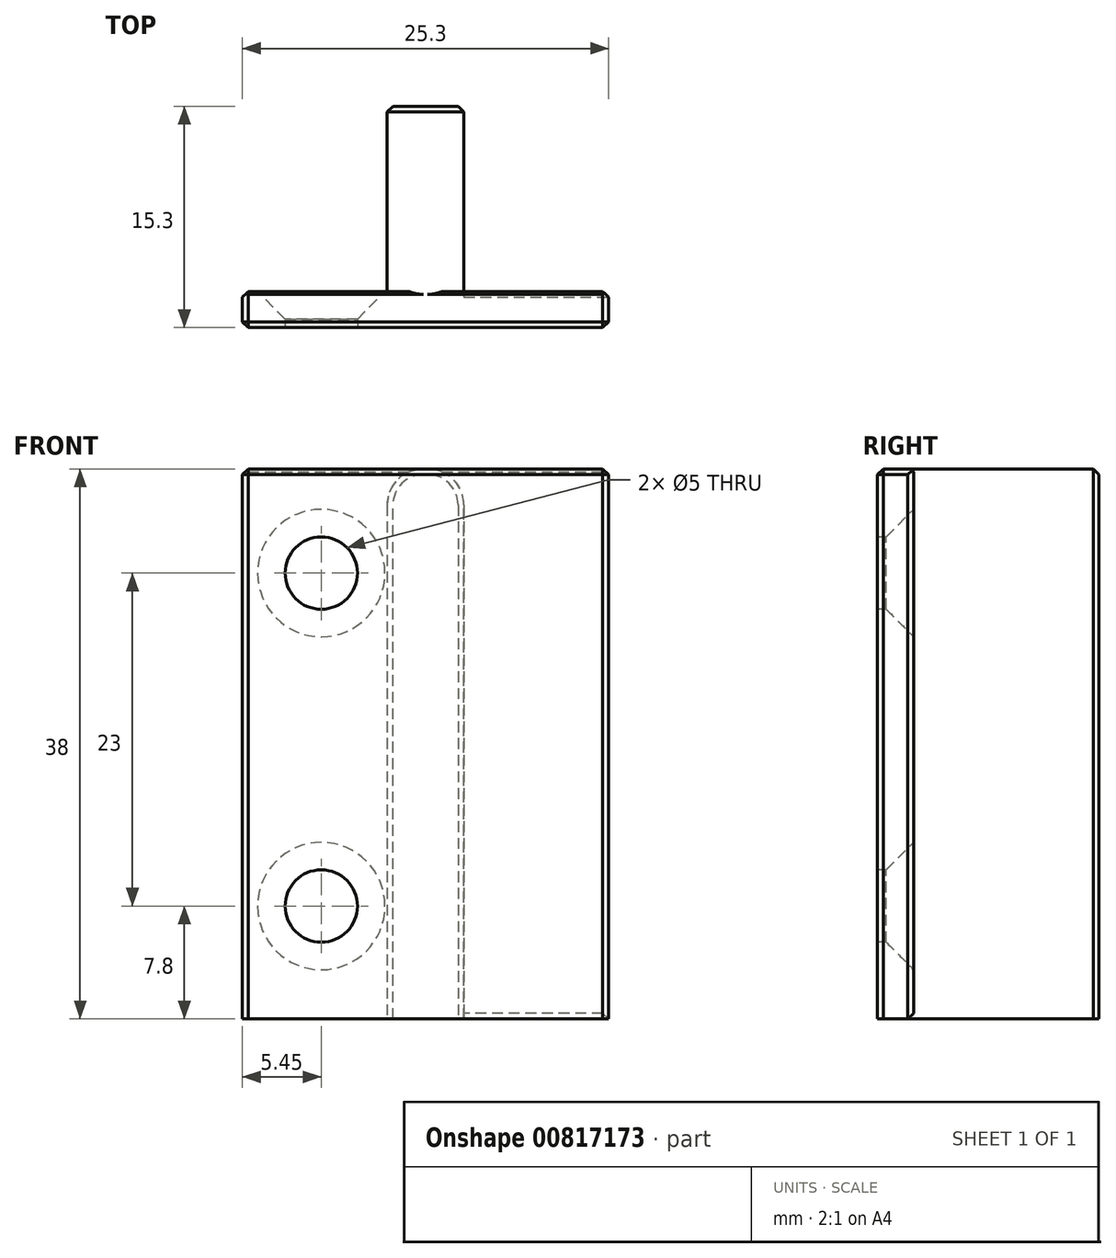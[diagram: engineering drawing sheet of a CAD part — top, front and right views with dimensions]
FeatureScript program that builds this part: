
annotation { "Feature Type Name" : "Feature", "Feature Type Description" : "" }
export const myFeature = defineFeature(function(context is Context, id is Id, definition is map)
    precondition{}
    {
        {
            var Q0;
            Q0=qCreatedBy(makeId("Top.planeOp"),FACE);
            var sketch = newSketch(context, id + "F0", { "sketchPlane" : qUnion([Q0])});
            skLineSegment(sketch, "E0", {"start": v(0, 15.3) * mm, "end": v(-2.65, 15.3) * mm});
            skLineSegment(sketch, "E1", {"start": v(-2.65, 15.3) * mm, "end": v(-2.65, 2.5) * mm});
            skLineSegment(sketch, "E2", {"start": v(-2.65, 2.5) * mm, "end": v(-12.65, 2.5) * mm});
            skLineSegment(sketch, "E3", {"start": v(-12.65, 2.5) * mm, "end": v(-12.65, 0) * mm});
            skLineSegment(sketch, "E4", {"start": v(-12.65, 0) * mm, "end": v(0, 0) * mm});
            skLineSegment(sketch, "E5", {"start": v(0, 26.2) * mm, "end": v(0, -20.62) * mm, "construction": true});
            skLineSegment(sketch, "E6.MirrorCS", {"start": v(0, 15.3) * mm, "end": v(2.65, 15.3) * mm});
            skLineSegment(sketch, "E7.MirrorCS", {"start": v(2.65, 15.3) * mm, "end": v(2.65, 2.5) * mm});
            skLineSegment(sketch, "E8.MirrorCS", {"start": v(2.65, 2.5) * mm, "end": v(12.65, 2.5) * mm});
            skLineSegment(sketch, "E9.MirrorCS", {"start": v(12.65, 0) * mm, "end": v(0, 0) * mm});
            skLineSegment(sketch, "E10.MirrorCS", {"start": v(12.65, 2.5) * mm, "end": v(12.65, 0) * mm});
            skLineSegment(sketch, "E11", {"start": v(-7.2, 6.99) * mm, "end": v(-7.2, -6.23) * mm, "construction": true});
            skSolve(sketch);
        }
        {
            var Q0;
            Q0=makeQuery(id+"F0.imprint","IMPRINT",FACE,{"disambiguationData":[TD([[makeQuery(id+"F0.imprint","IMPRINT",EDGE,{"derivedFrom":sQuery(id+"F0.wireOp",EDGE,"E0")}),1.0]])]});
            extrude(context, id + "F1", {"entities" : qUnion([Q0]), "depth" : 38 * mm, "offsetDistance" : 25 * mm});
        }
        {
            var Q0;
            Q0=qCreatedBy(makeId("Front.planeOp"),FACE);
            var sketch = newSketch(context, id + "F2", { "sketchPlane" : qUnion([Q0])});
            skLineSegment(sketch, "E12", {"start": v(-7.2, 0.13) * mm, "end": v(-7.2, 47.06) * mm, "construction": true});
            skLineSegment(sketch, "E13", {"start": v(0, 0) * mm, "end": v(0, 52.07) * mm, "construction": true});
            skCircle(sketch, "E14", {"center": v(-7.2, 7.8) * mm, "radius": 2.5 * mm});
            skCircle(sketch, "E15", {"center": v(-7.2, 30.8) * mm, "radius": 2.5 * mm});
            skCircle(sketch, "E16.MirrorC", {"center": v(7.2, 30.8) * mm, "radius": 2.5 * mm});
            skCircle(sketch, "E17.MirrorC", {"center": v(7.2, 7.8) * mm, "radius": 2.5 * mm});
            skSolve(sketch);
        }
        {
            var Q0;
            Q0=makeQuery(id+"F2.imprint","IMPRINT",FACE,{"disambiguationData":[TD([[makeQuery(id+"F2.imprint","IMPRINT",EDGE,{"derivedFrom":sQuery(id+"F2.wireOp",EDGE,"E15")}),1.0]])]});
            var Q1;
            Q1=makeQuery(id+"F2.imprint","IMPRINT",FACE,{"disambiguationData":[TD([[makeQuery(id+"F2.imprint","IMPRINT",EDGE,{"derivedFrom":sQuery(id+"F2.wireOp",EDGE,"E14")}),1.0]])]});
            var Q2;
            Q2=makeQuery(id+"F2.imprint","IMPRINT",FACE,{"disambiguationData":[TD([[makeQuery(id+"F2.imprint","IMPRINT",EDGE,{"derivedFrom":sQuery(id+"F2.wireOp",EDGE,"E17.MirrorC")}),-1.0]])]});
            var Q3;
            Q3=makeQuery(id+"F2.imprint","IMPRINT",FACE,{"disambiguationData":[TD([[makeQuery(id+"F2.imprint","IMPRINT",EDGE,{"derivedFrom":sQuery(id+"F2.wireOp",EDGE,"E16.MirrorC")}),-1.0]])]});
            extrude(context, id + "F3", {"entities" : qUnion([Q0, Q1, Q2, Q3]), "operationType" : NewBodyOperationType.REMOVE, "oppositeDirection" : true, "depth" : 25 * mm, "offsetDistance" : 25 * mm});
        }
        {
            var Q0;
            Q0=makeQuery(id+"F3.boolean.opBoolean","INTERSECT",EDGE,{"derivedFrom":[makeQuery(id+"F1.opExtrude","SWEPT_FACE",FACE,{"disambiguationData":[OSD([sQuery(id+"F0.wireOp",EDGE,"E8.MirrorCS")])]}),makeQuery(id+"F3.opExtrude","SWEPT_FACE",FACE,{"disambiguationData":[OSD([sQuery(id+"F2.wireOp",EDGE,"E17.MirrorC")])]})]});
            var Q1;
            Q1=makeQuery(id+"F3.boolean.opBoolean","INTERSECT",EDGE,{"derivedFrom":[makeQuery(id+"F1.opExtrude","SWEPT_FACE",FACE,{"disambiguationData":[OSD([sQuery(id+"F0.wireOp",EDGE,"E8.MirrorCS")])]}),makeQuery(id+"F3.opExtrude","SWEPT_FACE",FACE,{"disambiguationData":[OSD([sQuery(id+"F2.wireOp",EDGE,"E16.MirrorC")])]})]});
            var Q2;
            Q2=makeQuery(id+"F3.boolean.opBoolean","INTERSECT",EDGE,{"derivedFrom":[makeQuery(id+"F1.opExtrude","SWEPT_FACE",FACE,{"disambiguationData":[OSD([sQuery(id+"F0.wireOp",EDGE,"E2")])]}),makeQuery(id+"F3.opExtrude","SWEPT_FACE",FACE,{"disambiguationData":[OSD([sQuery(id+"F2.wireOp",EDGE,"E14")])]})]});
            var Q3;
            Q3=makeQuery(id+"F3.boolean.opBoolean","INTERSECT",EDGE,{"derivedFrom":[makeQuery(id+"F1.opExtrude","SWEPT_FACE",FACE,{"disambiguationData":[OSD([sQuery(id+"F0.wireOp",EDGE,"E2")])]}),makeQuery(id+"F3.opExtrude","SWEPT_FACE",FACE,{"disambiguationData":[OSD([sQuery(id+"F2.wireOp",EDGE,"E15")])]})]});
            chamfer(context, id + "F4", {"entities" : qUnion([Q0, Q1, Q2, Q3]), "width" : 1.9 * mm, "tangentPropagation" : true});
        }
        {
            var Q0;
            Q0=makeQuery(id+"F1.opExtrude","CAP_EDGE",EDGE,{"disambiguationData":[OSD([sQuery(id+"F0.wireOp",EDGE,"E1")])],"isStart":false});
            var Q1;
            Q1=makeQuery(id+"F1.opExtrude","CAP_EDGE",EDGE,{"disambiguationData":[OSD([sQuery(id+"F0.wireOp",EDGE,"E7.MirrorCS")])],"isStart":false});
            fillet(context, id + "F5", {"entities" : qUnion([Q0, Q1]), "radius" : 2.5 * mm, "tangentPropagation" : true, "allowEdgeOverflow" : false});
        }
        {
            var Q0;
            Q0=makeQuery(id+"F1.opExtrude","SWEPT_EDGE",EDGE,{"disambiguationData":[OSD([sQuery(id+"F0.wireOp",EDGE,"E0"),sQuery(id+"F0.wireOp",EDGE,"E1")])]});
            var Q1;
            Q1=makeQuery(id+"F1.opExtrude","SWEPT_EDGE",EDGE,{"disambiguationData":[OSD([sQuery(id+"F0.wireOp",EDGE,"E6.MirrorCS"),sQuery(id+"F0.wireOp",EDGE,"E7.MirrorCS")])]});
            var Q2;
            Q2=makeQuery(id+"F1.opExtrude","CAP_EDGE",EDGE,{"disambiguationData":[OSD([sQuery(id+"F0.wireOp",EDGE,"E8.MirrorCS")])],"isStart":true});
            var Q3;
            Q3=makeQuery(id+"F1.opExtrude","SWEPT_EDGE",EDGE,{"disambiguationData":[OSD([sQuery(id+"F0.wireOp",EDGE,"E8.MirrorCS"),sQuery(id+"F0.wireOp",EDGE,"E10.MirrorCS")])]});
            var Q4;
            Q4=makeQuery(id+"F1.opExtrude","CAP_EDGE",EDGE,{"disambiguationData":[OSD([sQuery(id+"F0.wireOp",EDGE,"E4"),sQuery(id+"F0.wireOp",EDGE,"E9.MirrorCS")])],"isStart":false});
            var Q5;
            Q5=makeQuery(id+"F1.opExtrude","SWEPT_EDGE",EDGE,{"disambiguationData":[OSD([sQuery(id+"F0.wireOp",EDGE,"E9.MirrorCS"),sQuery(id+"F0.wireOp",EDGE,"E10.MirrorCS")])]});
            var Q6;
            Q6=makeQuery(id+"F1.opExtrude","SWEPT_EDGE",EDGE,{"disambiguationData":[OSD([sQuery(id+"F0.wireOp",EDGE,"E2"),sQuery(id+"F0.wireOp",EDGE,"E3")])]});
            var Q7;
            Q7=makeQuery(id+"F1.opExtrude","SWEPT_EDGE",EDGE,{"disambiguationData":[OSD([sQuery(id+"F0.wireOp",EDGE,"E3"),sQuery(id+"F0.wireOp",EDGE,"E4")])]});
            var Q8;
            Q8=makeQuery(id+"F1.opExtrude","CAP_EDGE",EDGE,{"disambiguationData":[OSD([sQuery(id+"F0.wireOp",EDGE,"E3")])],"isStart":false});
            var Q9;
            Q9=makeQuery(id+"F1.opExtrude","CAP_EDGE",EDGE,{"disambiguationData":[OSD([sQuery(id+"F0.wireOp",EDGE,"E10.MirrorCS")])],"isStart":false});
            chamfer(context, id + "F6", {"entities" : qUnion([Q0, Q1, Q2, Q3, Q4, Q5, Q6, Q7, Q8, Q9]), "width" : 0.4 * mm, "tangentPropagation" : true});
        }
        {
            var Q0;
            Q0=makeQuery(id+"F1.opExtrude","CAP_EDGE",EDGE,{"disambiguationData":[OSD([sQuery(id+"F0.wireOp",EDGE,"E8.MirrorCS")])],"isStart":false});
            var Q1;
            Q1=makeQuery(id+"F1.opExtrude","CAP_EDGE",EDGE,{"disambiguationData":[OSD([sQuery(id+"F0.wireOp",EDGE,"E2")])],"isStart":false});
            chamfer(context, id + "F7", {"entities" : qUnion([Q0, Q1]), "width" : 0.2 * mm, "tangentPropagation" : true});
        }
    });
